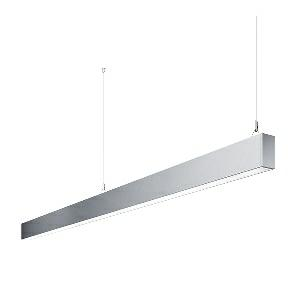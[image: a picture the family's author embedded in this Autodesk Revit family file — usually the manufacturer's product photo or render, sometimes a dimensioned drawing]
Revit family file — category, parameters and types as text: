
# Revit family: dotoo_line_-_dlp_3000_840_d_end_00805832_191c
name_source: partatom
category: Lighting Fixtures
units: mm (PartAtom-declared; Revit-internal decimal feet)

## family parameters
Cut with Voids When Loaded = No
Host = Face
Light Source = No
Part Type = Normal
Room Calculation Point = No
Round Connector Dimension = Use Diameter
Shared = No

## types (1)
- DOTOO.line - DLP 3000/840/D END (1 x LED, 2750 lm, 4000K)
    Apparent Load = 26 VA
    Approval mark = CE
    CIE Flux Codes = 67 91 98 100 100
    Color Rendering = 80-89
    Color Temperature = 4000K
    Control Gear = Electronic ballast
    Default Elevation = 1800 mm
    Description = DLP 3000/840/D|Suspended luminaire|light source: LED|connected load: 220-240 V, 50/60 Hz|Power consumption: approx. 26 W|standby: approx. 0,15|luminous flux: 2750 lm|luminous efficacy: 105 lm/W|light distribution: Direct|direct ratio: approx. 100 %|colour temperature: Cold white, ca. 4000 K|color rendering index (CRI): >= 80|chromaticity tolerance:  3 SDCM|System of protection: IP 40|technology: Continuously dimmable|luminaire body|material: Sectional aluminium|colour: Silver|lamp cover: Acrylic (PMMA), Clear|mains lead: 1,0 m With free stranded wires|Fastening: Steel cable 0.3 - 0.7 m|glare control: Prism aperture|luminance(L65): <= 3000 cd/m|unified glare rating(4H 8H): <=  19|special features: DALI Load 1x, TouchDIM - dimming via standard switch, Through-wired, up to 18 m on one mains connection, Flicker-free, Suitable as emergency lighting, Mechanical and electrical connection of the individual modules without tools|
    Frequency = 50 Hz
    Height = 110 mm
    Lamp = 1 x LED
    Lamp Light Flux = 2750 lm
    Lamp count = 1
    Length = 2250 mm
    Luminous efficacy = 106 lm/W
    Manufacturer = Waldmann
    ModVariant = No
    Model = 00805832
    Mounting Place = Ceiling
    Mounting Type = Pendant
    Number of Poles = 1
    OnlyDefault = Yes
    Power Factor = 1
    Product Name = DOTOO.line - DLP 3000/840/D END
    Product group = Suspended luminaire
    ProductGroupID = 9
    Protection Class = Protection class I
    Protection Degree = IP 40
    RLX_Detail_Level = 1
    RLX_Emergency_Light_Flux = 0 lm
    RLX_Emergency_Type = 0
    RLX_Emergency_Type_DB = No
    RlxData = <blob elided: 23073 chars, md5=6e169b59>
    Socket = socket
    Standby Power = 0 W
    System Light Flux = 2750 lm
    System Power = 26 W
    Type Comments = Product without accessories
    Type Image = 113318000-00692621.jpg
    URL = http://relux.com
    VarID = ---
    Voltage = 230 V
    Voltage Range = 220-240 V
    Weight = 0.00 kg
    Width = 60 mm  [stored 0.19685 ft]

note: [stored X ft] marks values corroborated as IEEE doubles in the binary element streams (Revit-internal decimal feet)

## geometry (parser evidence)
native form markers: Blend x4, Sweep x13
no freeform markers — native parametric forms only
